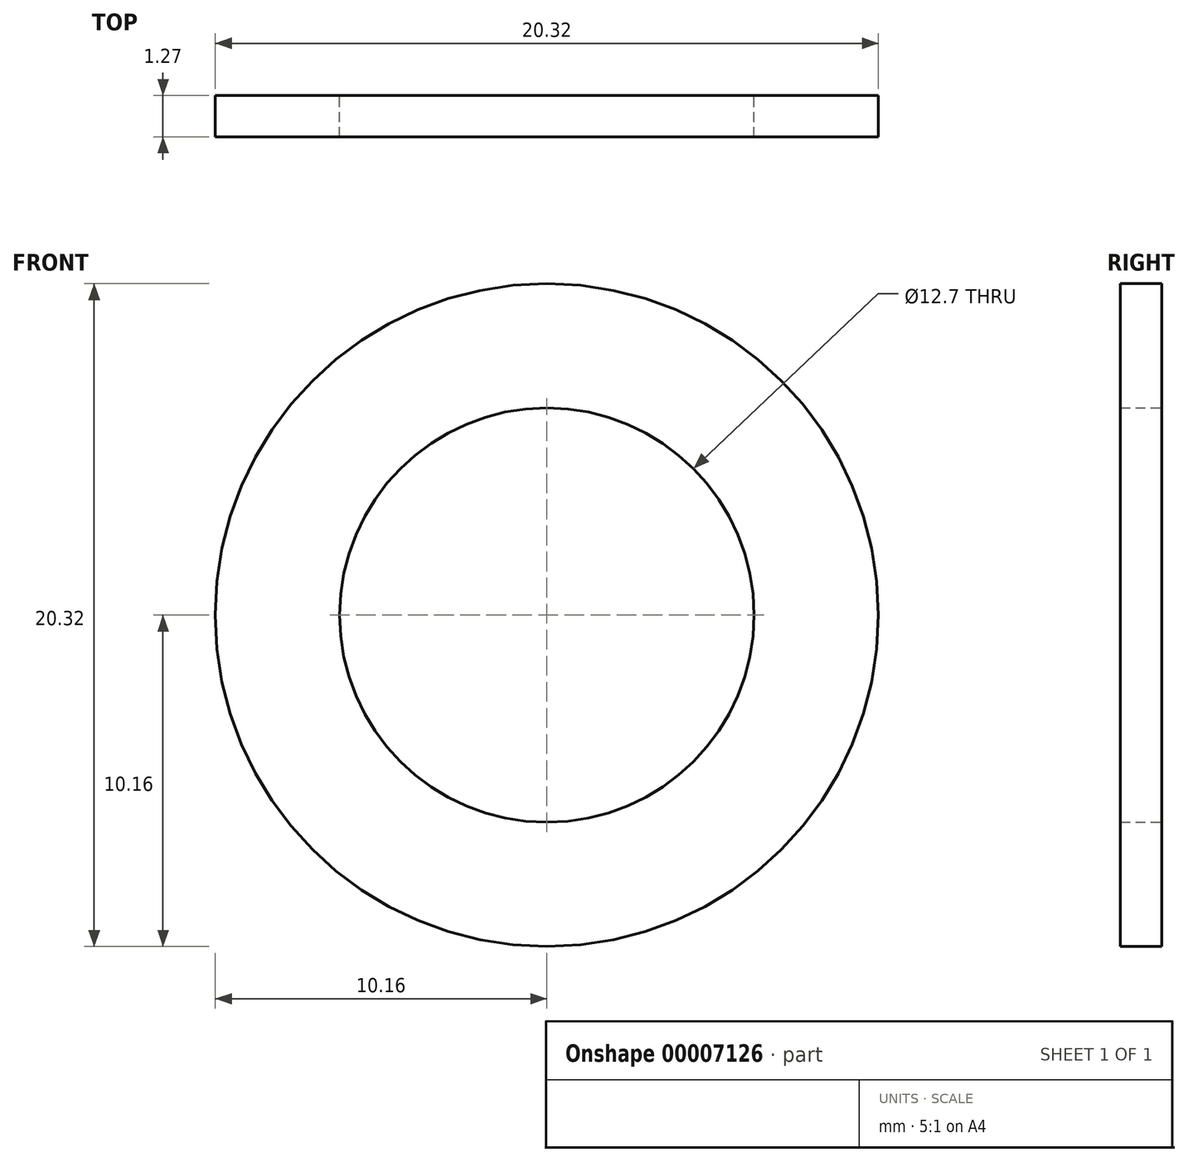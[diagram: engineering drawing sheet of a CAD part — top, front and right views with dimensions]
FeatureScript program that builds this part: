
annotation { "Feature Type Name" : "Feature", "Feature Type Description" : "" }
export const myFeature = defineFeature(function(context is Context, id is Id, definition is map)
    precondition{}
    {
        {
            var Q0;
            Q0=qCreatedBy(makeId("Front.planeOp"),FACE);
            var sketch = newSketch(context, id + "F0", { "sketchPlane" : qUnion([Q0])});
            skCircle(sketch, "E0", {"center": v(0, 0) * mm, "radius": 10.16 * mm});
            skCircle(sketch, "E1", {"center": v(0, 0) * mm, "radius": 6.35 * mm});
            skSolve(sketch);
        }
        {
            var Q0;
            Q0=makeQuery(id+"F0.imprint","IMPRINT",FACE,{"disambiguationData":[TD([[makeQuery(id+"F0.imprint","IMPRINT",EDGE,{"derivedFrom":sQuery(id+"F0.wireOp",EDGE,"E0")}),1.0]])]});
            extrude(context, id + "F1", {"entities" : qUnion([Q0]), "depth" : 1.27 * mm});
        }
    });
